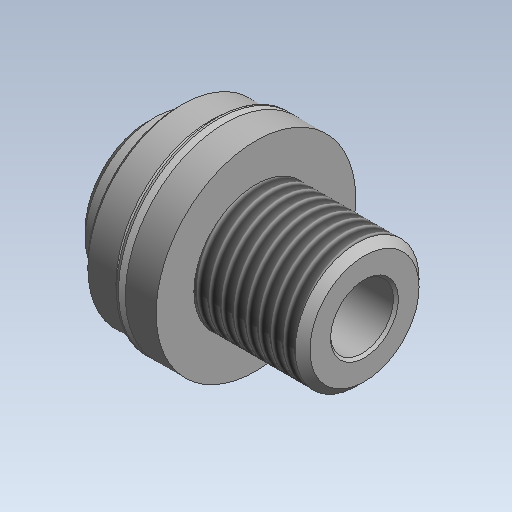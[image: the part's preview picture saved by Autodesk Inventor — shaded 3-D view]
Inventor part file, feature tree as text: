
AUTODESK INVENTOR PART (.ipt)
format: ipt  version: 2020 (Build 240168000, 168)  size: 232,448 bytes
history: native  units: mm (DEFAULTED — no unit token found)
features: other x84, sketch x5, revolve x4, thread x1, hole x1
ambient origin geometry x8: Origin, YZ Plane, XZ Plane, XY Plane, X Axis, Y Axis, Z Axis, Center Point
bodies: Solid1 (feature_tree)
feature tree (95):
  revolve  "Revolution1"  [1 undecoded]
  thread  "Thread1"  [1 undecoded]
  revolve  "Revolution2"  Angle=360.0deg
  revolve  "Revolution3"  [1 undecoded]
  hole  "Hole1"  [1 undecoded]
  revolve  "Revolution4"  [1 undecoded]
  other  "hh_XY"
  other  "hh_YZ"
  other  "hh_ZX"
  other  "hh_X"
  other  "hh_Y"
  other  "hh_Z"
  other  "hh_Center"
  other  "rod_guide_XY"
  other  "rod_guide_YZ"
  other  "rod_guide_ZX"
  other  "rod_guide_X"
  other  "rod_guide_Y"
  other  "rod_guide_Z"
  other  "rod_guide_Center"
  other  "t1_XY"
  other  "t1_YZ"
  other  "t1_ZX"
  other  "t1_X"
  other  "t1_Y"
  other  "t1_Z"
  other  "t1_Center"
  other  "t111_XY"
  other  "t111_YZ"
  other  "t111_ZX"
  other  "t111_X"
  other  "t111_Y"
  other  "t111_Z"
  other  "t111_Center"
  other  "to_foot_bracket_XY"
  other  "to_foot_bracket_YZ"
  other  "to_foot_bracket_ZX"
  other  "to_foot_bracket_X"
  other  "to_foot_bracket_Y"
  other  "to_foot_bracket_Z"
  other  "to_foot_bracket_Center"
  other  "to_nut_XY"
  other  "to_nut_YZ"
  other  "to_nut_ZX"
  other  "to_nut_X"
  other  "to_nut_Y"
  other  "to_nut_Z"
  other  "to_nut_Center"
  other  "to_rod_XY"
  other  "to_rod_YZ"
  other  "to_rod_ZX"
  other  "to_rod_X"
  other  "to_rod_Y"
  other  "to_rod_Z"
  other  "to_rod_Center"
  other  "to_screw_XY"
  other  "to_screw_YZ"
  other  "to_screw_ZX"
  other  "to_screw_X"
  other  "to_screw_Y"
  other  "to_screw_Z"
  other  "to_screw_Center"
  other  "to_trunnion_brackets_XY"
  other  "to_trunnion_brackets_YZ"
  other  "to_trunnion_brackets_ZX"
  other  "to_trunnion_brackets_X"
  other  "to_trunnion_brackets_Y"
  other  "to_trunnion_brackets_Z"
  other  "to_trunnion_brackets_Center"
  other  "to_trunnion_brackets1_XY"
  other  "to_trunnion_brackets1_YZ"
  other  "to_trunnion_brackets1_ZX"
  other  "to_trunnion_brackets1_X"
  other  "to_trunnion_brackets1_Y"
  other  "to_trunnion_brackets1_Z"
  other  "to_trunnion_brackets1_Center"
  other  "to_trunnion_brackets2_XY"
  other  "to_trunnion_brackets2_YZ"
  other  "to_trunnion_brackets2_ZX"
  other  "to_trunnion_brackets2_X"
  other  "to_trunnion_brackets2_Y"
  other  "to_trunnion_brackets2_Z"
  other  "to_trunnion_brackets2_Center"
  other  "to_tube_XY"
  other  "to_tube_YZ"
  other  "to_tube_ZX"
  other  "to_tube_X"
  other  "to_tube_Y"
  other  "to_tube_Z"
  other  "to_tube_Center"
  sketch  "Sketch_1"  dims[d0=360.0deg d1=10.3695mm d2=0.0mm d3=360.0deg]
  sketch  "Sketch_3"  dims[d4=360.0deg]
  sketch  "Sketch_4"  dims[d5=6.4389mm d6=6.0mm d7=6.9469mm d8=2.0mm d9=90.0deg d10=22.225mm d11=0.0mm d12=360.0deg]
  sketch  "Sketch4"  dims[d13=0.0mm d14=0.0mm d15=0.0mm d16=0.0mm d17=0.0mm d18=0.0mm]
  sketch  "Sketch_47"
note: 5 required parameter values undecoded (feature->parameter linkage not recoverable at this tier; creation-order binding heuristic only, values carry confidence <= 0.55)